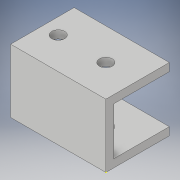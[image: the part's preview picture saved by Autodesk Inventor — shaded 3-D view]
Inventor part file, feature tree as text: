
AUTODESK INVENTOR PART (.ipt)
format: ipt  version: 2018 (Build 220112000, 112)  size: 122,880 bytes
history: native  units: in
note: dims shown in document units (in); Inventor stores cm internally (conversion verified against a paired STEP export)
features: extrude x3, sketch x3, projected_geometry x1
ambient origin geometry x8: Origin, YZ Plane, XZ Plane, XY Plane, X Axis, Y Axis, Z Axis, Center Point
bodies: Solid1 (feature_tree)
feature tree (7):
  extrude  "Extrusion1"  Depth=0.125in
  sketch  "Sketch2"  dims[d2=1.0in d3=0.0in d4=0.125in]
  sketch  "Sketch3"  dims[d7=0.5in d8=0.75in]
  extrude  "Extrusion3"  Depth=0.75in
  extrude  "Extrusion4"  Depth=0.2031in
  projected_geometry  "Projected Loop1"
  sketch  "Sketch4"  dims[d9=0.2031in d10=0.2031in d11=2.5in d12=0.0in d13=5.0in d14=0.0in]
